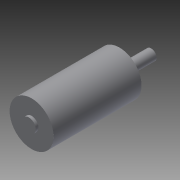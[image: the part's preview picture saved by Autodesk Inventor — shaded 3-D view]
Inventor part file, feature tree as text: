
AUTODESK INVENTOR PART (.ipt)
format: ipt  version: 2013 (Build 170138000, 138)  size: 110,080 bytes
history: native  units: mm
features: extrude x5, sketch x5, hole x1
ambient origin geometry x8: Origin, YZ Plane, XZ Plane, XY Plane, X Axis, Y Axis, Z Axis, Center Point
bodies: Solid1 (feature_tree)
feature tree (11):
  extrude  "Extrusion1"  Depth=32.0mm TaperAngle=0.0deg
  sketch  "Sketch2"  dims[d3=6.0mm d4=5.5mm]
  extrude  "Extrusion2"  Depth=5.5mm
  hole  "Hole1"  [1 undecoded]
  extrude  "Extrusion3"  Depth=4.0mm
  extrude  "Extrusion4"  Depth=1.0mm
  extrude  "Extrusion5"  Depth=1.0mm
  sketch  "Sketch1"  dims[d0=16.0mm d1=32.0mm d2=0.0mm]
  sketch  "Sketch3"  dims[d5=20.0mm d7=360.0deg d9=1.5mm d10=0.0mm]
  sketch  "Sketch4"  dims[d11=1.567mm d12=3.0mm d13=12.24mm d14=3.58mm d15=90.0deg d16=3.0mm d17=20.594885mm d18=4.0mm]
  sketch  "Sketch5"  dims[d19=10.0mm d20=0.0mm d21=1.0mm d23=1.0mm d24=7.5mm d25=0.0mm d26=5.0mm d27=1.0mm d28=0.0mm]
note: 1 required parameter value undecoded (feature->parameter linkage not recoverable at this tier; creation-order binding heuristic only, values carry confidence <= 0.55)
